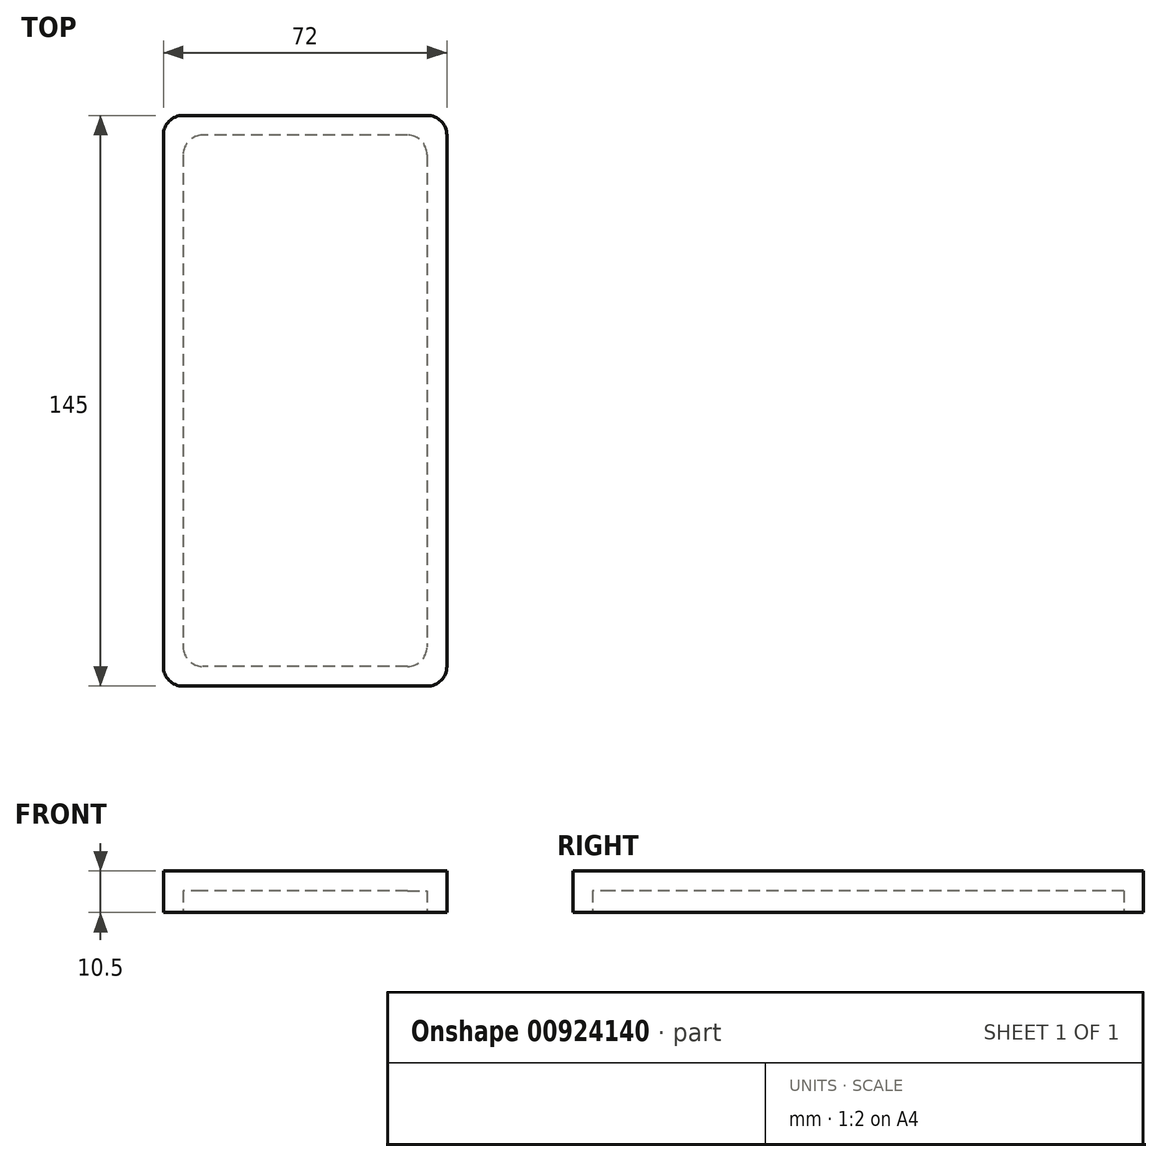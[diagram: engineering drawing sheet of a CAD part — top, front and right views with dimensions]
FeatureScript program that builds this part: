
annotation { "Feature Type Name" : "Feature", "Feature Type Description" : "" }
export const myFeature = defineFeature(function(context is Context, id is Id, definition is map)
    precondition{}
    {
        {
            var Q0;
            Q0=qCreatedBy(makeId("Right.planeOp"),FACE);
            var sketch = newSketch(context, id + "F0", { "sketchPlane" : qUnion([Q0])});
            skLineSegment(sketch, "E0.bottom", {"start": v(72.5, -5.25) * mm, "end": v(-72.5, -5.25) * mm});
            skLineSegment(sketch, "E0.top", {"start": v(72.5, 5.25) * mm, "end": v(-72.5, 5.25) * mm});
            skLineSegment(sketch, "E0.left", {"start": v(72.5, -5.25) * mm, "end": v(72.5, 5.25) * mm});
            skLineSegment(sketch, "E0.right", {"start": v(-72.5, -5.25) * mm, "end": v(-72.5, 5.25) * mm});
            skPoint(sketch, "E0.middle", {"position": v(0, 0) * mm});
            skSolve(sketch);
        }
        {
            var Q0;
            Q0=makeQuery(id+"F0.imprint","IMPRINT",FACE,{"disambiguationData":[TD([[makeQuery(id+"F0.imprint","IMPRINT",EDGE,{"derivedFrom":sQuery(id+"F0.wireOp",EDGE,"E0.bottom")}),-1.0]])]});
            extrude(context, id + "F1", {"entities" : qUnion([Q0]), "endBound" : BoundingType.SYMMETRIC, "depth" : 72 * mm, "offsetDistance" : 25 * mm});
        }
        {
            var Q0;
            Q0=makeQuery(id+"F1.opExtrude","CAP_EDGE",EDGE,{"disambiguationData":[OSD([sQuery(id+"F0.wireOp",EDGE,"E0.right")])],"isStart":false});
            var Q1;
            Q1=makeQuery(id+"F1.opExtrude","CAP_EDGE",EDGE,{"disambiguationData":[OSD([sQuery(id+"F0.wireOp",EDGE,"E0.left")])],"isStart":false});
            var Q2;
            Q2=makeQuery(id+"F1.opExtrude","CAP_EDGE",EDGE,{"disambiguationData":[OSD([sQuery(id+"F0.wireOp",EDGE,"E0.right")])],"isStart":true});
            var Q3;
            Q3=makeQuery(id+"F1.opExtrude","CAP_EDGE",EDGE,{"disambiguationData":[OSD([sQuery(id+"F0.wireOp",EDGE,"E0.left")])],"isStart":true});
            fillet(context, id + "F2", {"entities" : qUnion([Q0, Q1, Q2, Q3]), "radius" : 5 * mm, "tangentPropagation" : true, "allowEdgeOverflow" : false});
        }
        {
            var Q0;
            Q0=makeQuery(id+"F1.opExtrude","SWEPT_FACE",FACE,{"disambiguationData":[OSD([sQuery(id+"F0.wireOp",EDGE,"E0.bottom")])]});
            shell(context, id + "F3", {"entities" : qUnion([Q0]), "thickness" : 5 * mm});
        }
        {
            var Q0;
            {var subQ0=sQuery(id+"F0.wireOp",EDGE,"E0.right");var subQ1=makeQuery(id+"F1.opExtrude","CAP_EDGE",EDGE,{"disambiguationData":[OSD([subQ0])],"isStart":true});var subQ2=sQuery(id+"F0.wireOp",EDGE,"E0.left");var subQ3=sQuery(id+"F0.wireOp",EDGE,"E0.top");var subQ4=sQuery(id+"F0.wireOp",EDGE,"E0.bottom");Q0=makeQuery(id+"F3.opShell","OFFSET_EDGE",EDGE,{"disambiguationData":[OSD([subQ4,subQ3,subQ2,subQ0]),TDD([makeQuery(id+"F2.opFillet","BLEND_EDGE",EDGE,{"blendedFrom":[subQ1,makeQuery(id+"F1.opExtrude","CAP_FACE",FACE,{"disambiguationData":[OSD([subQ4,subQ3,subQ2,subQ0])],"isStart":true})],"blendedInto":[makeQuery(id+"F1.opExtrude","CAP_FACE",FACE,{"disambiguationData":[OSD([subQ4,subQ3,subQ2,subQ0])],"isStart":true})]}),makeQuery(id+"F2.opFillet","BLEND_EDGE",EDGE,{"blendedFrom":[subQ1,makeQuery(id+"F1.opExtrude","SWEPT_FACE",FACE,{"disambiguationData":[OSD([subQ0])]})],"blendedInto":[makeQuery(id+"F1.opExtrude","SWEPT_FACE",FACE,{"disambiguationData":[OSD([subQ0])]})]})])]});}
            var Q1;
            {var subQ0=sQuery(id+"F0.wireOp",EDGE,"E0.right");var subQ1=makeQuery(id+"F1.opExtrude","CAP_EDGE",EDGE,{"disambiguationData":[OSD([subQ0])],"isStart":false});var subQ2=sQuery(id+"F0.wireOp",EDGE,"E0.left");var subQ3=sQuery(id+"F0.wireOp",EDGE,"E0.top");var subQ4=sQuery(id+"F0.wireOp",EDGE,"E0.bottom");Q1=makeQuery(id+"F3.opShell","OFFSET_EDGE",EDGE,{"disambiguationData":[OSD([subQ4,subQ3,subQ2,subQ0]),TDD([makeQuery(id+"F2.opFillet","BLEND_EDGE",EDGE,{"blendedFrom":[subQ1,makeQuery(id+"F1.opExtrude","CAP_FACE",FACE,{"disambiguationData":[OSD([subQ4,subQ3,subQ2,subQ0])],"isStart":false})],"blendedInto":[makeQuery(id+"F1.opExtrude","CAP_FACE",FACE,{"disambiguationData":[OSD([subQ4,subQ3,subQ2,subQ0])],"isStart":false})]}),makeQuery(id+"F2.opFillet","BLEND_EDGE",EDGE,{"blendedFrom":[subQ1,makeQuery(id+"F1.opExtrude","SWEPT_FACE",FACE,{"disambiguationData":[OSD([subQ0])]})],"blendedInto":[makeQuery(id+"F1.opExtrude","SWEPT_FACE",FACE,{"disambiguationData":[OSD([subQ0])]})]})])]});}
            var Q2;
            {var subQ0=sQuery(id+"F0.wireOp",EDGE,"E0.left");var subQ1=makeQuery(id+"F1.opExtrude","CAP_EDGE",EDGE,{"disambiguationData":[OSD([subQ0])],"isStart":true});var subQ2=sQuery(id+"F0.wireOp",EDGE,"E0.right");var subQ3=sQuery(id+"F0.wireOp",EDGE,"E0.top");var subQ4=sQuery(id+"F0.wireOp",EDGE,"E0.bottom");Q2=makeQuery(id+"F3.opShell","OFFSET_EDGE",EDGE,{"disambiguationData":[OSD([subQ4,subQ3,subQ0,subQ2]),TDD([makeQuery(id+"F2.opFillet","BLEND_EDGE",EDGE,{"blendedFrom":[subQ1,makeQuery(id+"F1.opExtrude","CAP_FACE",FACE,{"disambiguationData":[OSD([subQ4,subQ3,subQ0,subQ2])],"isStart":true})],"blendedInto":[makeQuery(id+"F1.opExtrude","CAP_FACE",FACE,{"disambiguationData":[OSD([subQ4,subQ3,subQ0,subQ2])],"isStart":true})]}),makeQuery(id+"F2.opFillet","BLEND_EDGE",EDGE,{"blendedFrom":[subQ1,makeQuery(id+"F1.opExtrude","SWEPT_FACE",FACE,{"disambiguationData":[OSD([subQ0])]})],"blendedInto":[makeQuery(id+"F1.opExtrude","SWEPT_FACE",FACE,{"disambiguationData":[OSD([subQ0])]})]})])]});}
            var Q3;
            {var subQ0=sQuery(id+"F0.wireOp",EDGE,"E0.left");var subQ1=makeQuery(id+"F1.opExtrude","CAP_EDGE",EDGE,{"disambiguationData":[OSD([subQ0])],"isStart":false});var subQ2=sQuery(id+"F0.wireOp",EDGE,"E0.right");var subQ3=sQuery(id+"F0.wireOp",EDGE,"E0.top");var subQ4=sQuery(id+"F0.wireOp",EDGE,"E0.bottom");Q3=makeQuery(id+"F3.opShell","OFFSET_EDGE",EDGE,{"disambiguationData":[OSD([subQ4,subQ3,subQ0,subQ2]),TDD([makeQuery(id+"F2.opFillet","BLEND_EDGE",EDGE,{"blendedFrom":[subQ1,makeQuery(id+"F1.opExtrude","CAP_FACE",FACE,{"disambiguationData":[OSD([subQ4,subQ3,subQ0,subQ2])],"isStart":false})],"blendedInto":[makeQuery(id+"F1.opExtrude","CAP_FACE",FACE,{"disambiguationData":[OSD([subQ4,subQ3,subQ0,subQ2])],"isStart":false})]}),makeQuery(id+"F2.opFillet","BLEND_EDGE",EDGE,{"blendedFrom":[subQ1,makeQuery(id+"F1.opExtrude","SWEPT_FACE",FACE,{"disambiguationData":[OSD([subQ0])]})],"blendedInto":[makeQuery(id+"F1.opExtrude","SWEPT_FACE",FACE,{"disambiguationData":[OSD([subQ0])]})]})])]});}
            fillet(context, id + "F4", {"entities" : qUnion([Q0, Q1, Q2, Q3]), "radius" : 5 * mm, "tangentPropagation" : true, "allowEdgeOverflow" : false});
        }
    });
